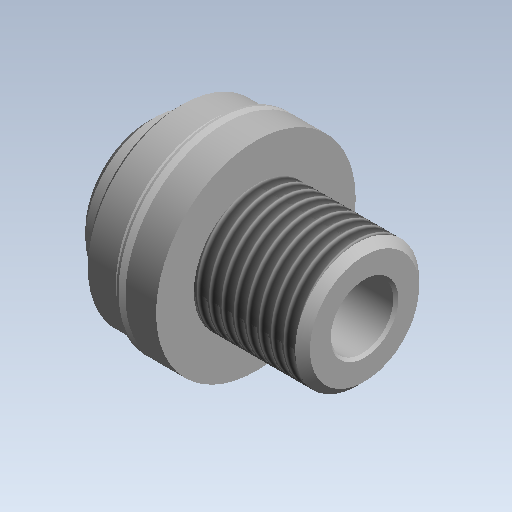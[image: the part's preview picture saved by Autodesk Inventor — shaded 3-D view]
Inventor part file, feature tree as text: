
AUTODESK INVENTOR PART (.ipt)
format: ipt  version: 2020 (Build 240168000, 168)  size: 231,424 bytes
history: native  units: mm (DEFAULTED — no unit token found)
features: other x84, sketch x5, revolve x4, thread x1, hole x1
ambient origin geometry x8: Origin, YZ Plane, XZ Plane, XY Plane, X Axis, Y Axis, Z Axis, Center Point
bodies: Solid1 (feature_tree)
feature tree (95):
  revolve  "Revolution1"  [1 undecoded]
  thread  "Thread1"  [1 undecoded]
  revolve  "Revolution2"  Angle=360.0deg
  revolve  "Revolution3"  [1 undecoded]
  hole  "Hole1"  [1 undecoded]
  revolve  "Revolution4"  [1 undecoded]
  other  "hh_XY"
  other  "hh_YZ"
  other  "hh_ZX"
  other  "hh_X"
  other  "hh_Y"
  other  "hh_Z"
  other  "hh_Center"
  other  "rod_guide_XY"
  other  "rod_guide_YZ"
  other  "rod_guide_ZX"
  other  "rod_guide_X"
  other  "rod_guide_Y"
  other  "rod_guide_Z"
  other  "rod_guide_Center"
  other  "t1_XY"
  other  "t1_YZ"
  other  "t1_ZX"
  other  "t1_X"
  other  "t1_Y"
  other  "t1_Z"
  other  "t1_Center"
  other  "t111_XY"
  other  "t111_YZ"
  other  "t111_ZX"
  other  "t111_X"
  other  "t111_Y"
  other  "t111_Z"
  other  "t111_Center"
  other  "to_foot_bracket_XY"
  other  "to_foot_bracket_YZ"
  other  "to_foot_bracket_ZX"
  other  "to_foot_bracket_X"
  other  "to_foot_bracket_Y"
  other  "to_foot_bracket_Z"
  other  "to_foot_bracket_Center"
  other  "to_nut_XY"
  other  "to_nut_YZ"
  other  "to_nut_ZX"
  other  "to_nut_X"
  other  "to_nut_Y"
  other  "to_nut_Z"
  other  "to_nut_Center"
  other  "to_rod_XY"
  other  "to_rod_YZ"
  other  "to_rod_ZX"
  other  "to_rod_X"
  other  "to_rod_Y"
  other  "to_rod_Z"
  other  "to_rod_Center"
  other  "to_screw_XY"
  other  "to_screw_YZ"
  other  "to_screw_ZX"
  other  "to_screw_X"
  other  "to_screw_Y"
  other  "to_screw_Z"
  other  "to_screw_Center"
  other  "to_trunnion_brackets_XY"
  other  "to_trunnion_brackets_YZ"
  other  "to_trunnion_brackets_ZX"
  other  "to_trunnion_brackets_X"
  other  "to_trunnion_brackets_Y"
  other  "to_trunnion_brackets_Z"
  other  "to_trunnion_brackets_Center"
  other  "to_trunnion_brackets1_XY"
  other  "to_trunnion_brackets1_YZ"
  other  "to_trunnion_brackets1_ZX"
  other  "to_trunnion_brackets1_X"
  other  "to_trunnion_brackets1_Y"
  other  "to_trunnion_brackets1_Z"
  other  "to_trunnion_brackets1_Center"
  other  "to_trunnion_brackets2_XY"
  other  "to_trunnion_brackets2_YZ"
  other  "to_trunnion_brackets2_ZX"
  other  "to_trunnion_brackets2_X"
  other  "to_trunnion_brackets2_Y"
  other  "to_trunnion_brackets2_Z"
  other  "to_trunnion_brackets2_Center"
  other  "to_tube_XY"
  other  "to_tube_YZ"
  other  "to_tube_ZX"
  other  "to_tube_X"
  other  "to_tube_Y"
  other  "to_tube_Z"
  other  "to_tube_Center"
  sketch  "Sketch_1"  dims[d0=360.0deg d1=10.3695mm d2=0.0mm d3=360.0deg]
  sketch  "Sketch_3"  dims[d4=360.0deg]
  sketch  "Sketch_4"  dims[d5=6.4389mm d6=6.0mm d7=6.9469mm d8=2.0mm d9=90.0deg d10=22.225mm d11=0.0mm d12=360.0deg]
  sketch  "Sketch4"  dims[d13=0.0mm d14=0.0mm d15=0.0mm d16=0.0mm d17=0.0mm d18=0.0mm]
  sketch  "Sketch_47"
note: 5 required parameter values undecoded (feature->parameter linkage not recoverable at this tier; creation-order binding heuristic only, values carry confidence <= 0.55)